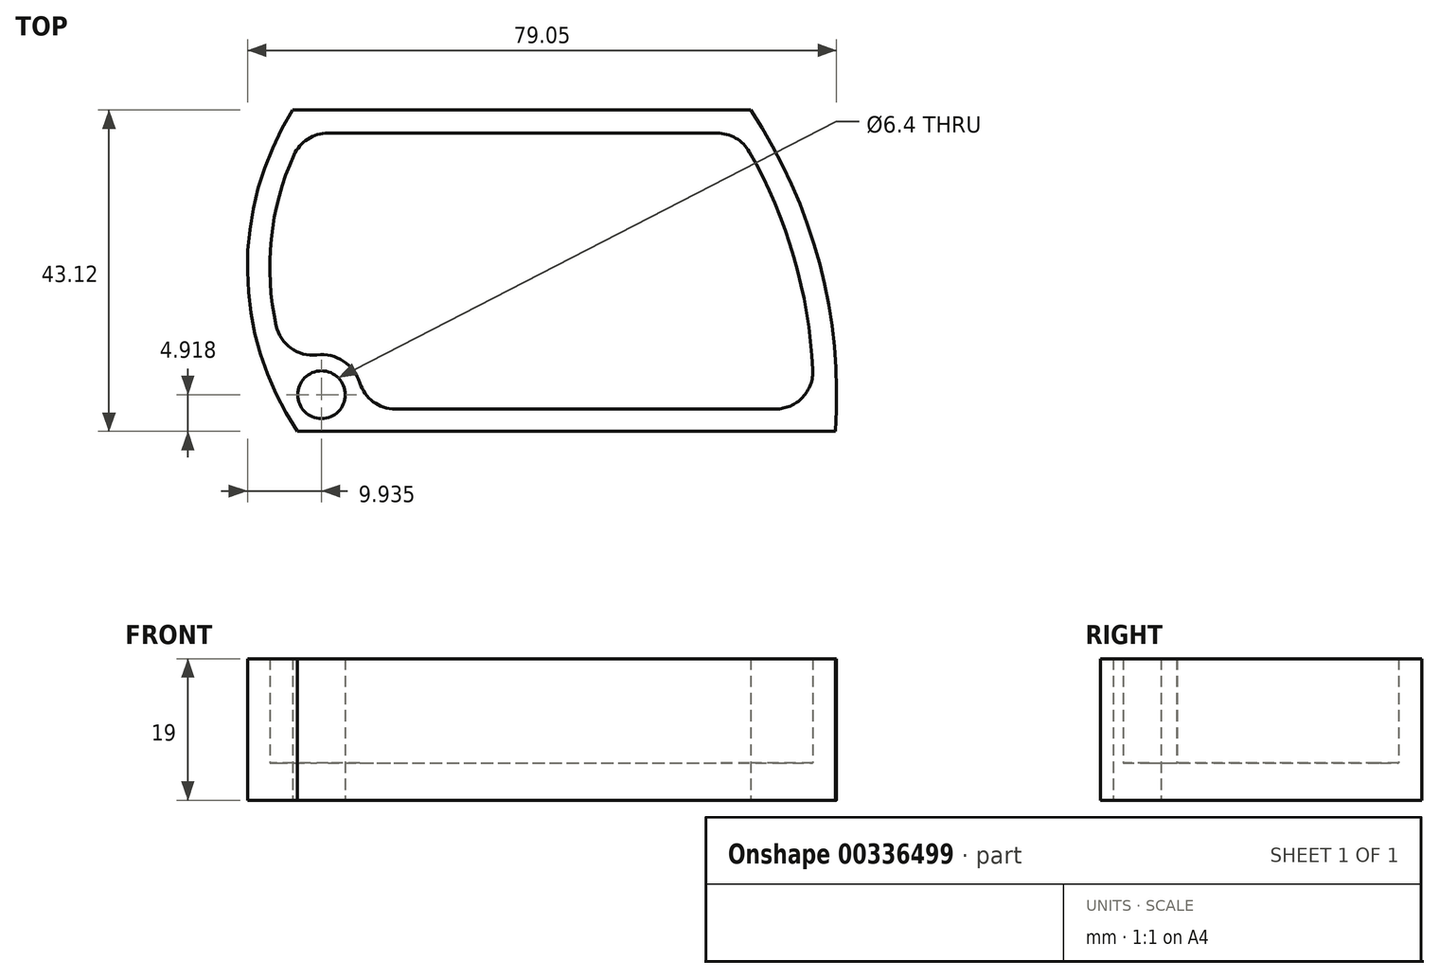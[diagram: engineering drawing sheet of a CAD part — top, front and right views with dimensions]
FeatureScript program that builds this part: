
annotation { "Feature Type Name" : "Feature", "Feature Type Description" : "" }
export const myFeature = defineFeature(function(context is Context, id is Id, definition is map)
    precondition{}
    {
        {
            var Q0;
            Q0=qCreatedBy(makeId("Top.planeOp"),FACE);
            var sketch = newSketch(context, id + "F0", { "sketchPlane" : qUnion([Q0])});
            skLineSegment(sketch, "E0.bottom", {"start": v(-77.52, 46.31) * mm, "end": v(-16.08, 46.31) * mm});
            skLineSegment(sketch, "E0.top", {"start": v(-76.94, 3.2) * mm, "end": v(-4.74, 3.2) * mm});
            skArc(sketch, "E1", {"start": v(-77.52, 46.31) * mm, "mid": v(-83.6, 24.67) * mm, "end": v(-76.94, 3.2) * mm});
            skArc(sketch, "E2", {"start": v(-4.74, 3.2) * mm, "mid": v(-6.84, 25.7) * mm, "end": v(-16.08, 46.31) * mm});
            skCircle(sketch, "E3", {"center": v(-73.68, 8.1) * mm, "radius": 3.2 * mm});
            skLineSegment(sketch, "E4.0", {"start": v(-72.8, 43.21) * mm, "end": v(-20.6, 43.21) * mm});
            skArc(sketch, "E4.1", {"start": v(-7.75, 11.45) * mm, "mid": v(-10.3, 26.56) * mm, "end": v(-16.26, 40.68) * mm});
            skLineSegment(sketch, "E5.0", {"start": v(-63.76, 6.2) * mm, "end": v(-12.74, 6.2) * mm});
            skArc(sketch, "E5.1", {"start": v(-77.37, 40.27) * mm, "mid": v(-80.41, 29) * mm, "end": v(-79.76, 17.35) * mm});
            skArc(sketch, "E6.filletArc", {"start": v(-72.8, 43.21) * mm, "mid": v(-75.52, 42.42) * mm, "end": v(-77.37, 40.27) * mm});
            skPoint(sketch, "E7.visualSharp", {"position": v(-17.77, 43.21) * mm});
            skArc(sketch, "E7.filletArc", {"start": v(-16.26, 40.68) * mm, "mid": v(-18.1, 42.54) * mm, "end": v(-20.6, 43.21) * mm});
            skArc(sketch, "E8.filletArc", {"start": v(-12.74, 6.2) * mm, "mid": v(-9.12, 7.75) * mm, "end": v(-7.75, 11.45) * mm});
            skArc(sketch, "E9", {"start": v(-68.53, 9.7) * mm, "mid": v(-70.74, 12.62) * mm, "end": v(-74.3, 13.46) * mm});
            skArc(sketch, "E10.filletArc", {"start": v(-79.76, 17.35) * mm, "mid": v(-77.78, 14.35) * mm, "end": v(-74.3, 13.46) * mm});
            skArc(sketch, "E11.filletArc", {"start": v(-68.53, 9.7) * mm, "mid": v(-66.72, 7.17) * mm, "end": v(-63.76, 6.2) * mm});
            skSolve(sketch);
        }
        {
            var Q0;
            Q0=makeQuery(id+"F0.imprint","IMPRINT",FACE,{"disambiguationData":[TD([[makeQuery(id+"F0.imprint","IMPRINT",EDGE,{"derivedFrom":sQuery(id+"F0.wireOp",EDGE,"E0.bottom")}),-1.0]])]});
            extrude(context, id + "F1", {"entities" : qUnion([Q0]), "depth" : 19 * mm});
        }
        {
            var Q0;
            Q0=makeQuery(id+"F0.imprint","IMPRINT",FACE,{"disambiguationData":[TD([[makeQuery(id+"F0.imprint","IMPRINT",EDGE,{"derivedFrom":sQuery(id+"F0.wireOp",EDGE,"E4.0")}),-1.0]])]});
            extrude(context, id + "F2", {"entities" : qUnion([Q0]), "operationType" : NewBodyOperationType.ADD, "depth" : 5 * mm});
        }
    });
